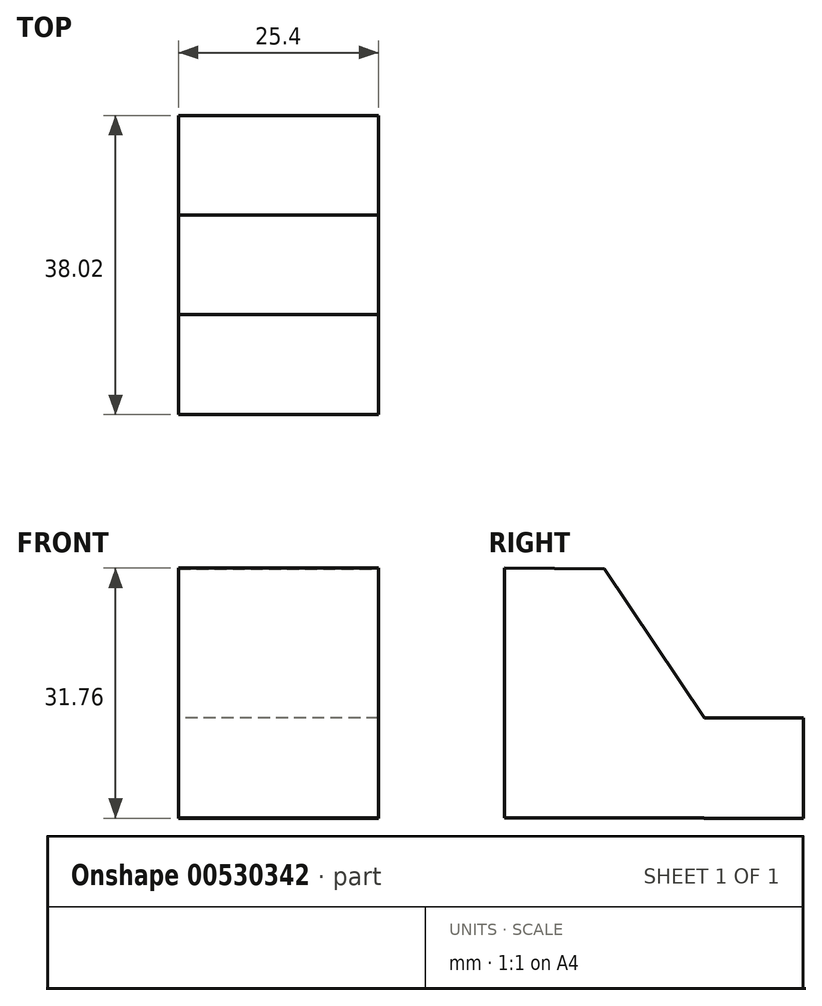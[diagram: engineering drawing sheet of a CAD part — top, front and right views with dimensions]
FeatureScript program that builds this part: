
annotation { "Feature Type Name" : "Feature", "Feature Type Description" : "" }
export const myFeature = defineFeature(function(context is Context, id is Id, definition is map)
    precondition{}
    {
        {
            var Q0;
            Q0=qCreatedBy(makeId("Right.planeOp"),FACE);
            var sketch = newSketch(context, id + "F0", { "sketchPlane" : qUnion([Q0])});
            skLineSegment(sketch, "E0", {"start": v(-45.87, 32.76) * mm, "end": v(-45.87, 1.01) * mm});
            skLineSegment(sketch, "E1", {"start": v(-45.87, 1.01) * mm, "end": v(-20.47, 1.01) * mm});
            skLineSegment(sketch, "E2", {"start": v(-20.47, 1.01) * mm, "end": v(-20.47, 32.56) * mm});
            skLineSegment(sketch, "E3", {"start": v(-45.87, 32.76) * mm, "end": v(-20.47, 32.56) * mm});
            skSolve(sketch);
        }
        {
            var Q0;
            Q0 = qSketchRegion(id + "F0", true);
            extrude(context, id + "F1", {"entities" : qUnion([Q0]), "depth" : 25.4 * mm, "offsetDistance" : 25.4 * mm});
        }
        {
            var Q0;
            Q0=makeQuery(id+"F1.opExtrude","CAP_FACE",FACE,{"disambiguationData":[OSD([sQuery(id+"F0.wireOp",EDGE,"E0"),sQuery(id+"F0.wireOp",EDGE,"E1"),sQuery(id+"F0.wireOp",EDGE,"E2"),sQuery(id+"F0.wireOp",EDGE,"E3")])],"isStart":false});
            var sketch = newSketch(context, id + "F2", { "sketchPlane" : qUnion([Q0])});
            skLineSegment(sketch, "E4", {"start": v(-33.17, 32.66) * mm, "end": v(-20.47, 13.71) * mm});
            skSolve(sketch);
        }
        {
            var Q0;
            Q0 = qSketchRegion(id + "F2", true);
            var Q1;
            {var subQ0=sQuery(id+"F2.wireOp",EDGE,"E4");Q1=makeQuery(id+"F2.imprint","IMPRINT",FACE,{"disambiguationData":[TD([[makeQuery(id+"F2.imprint","IMPRINT",EDGE,{"derivedFrom":subQ0}),1.0]])]});}
            extrude(context, id + "F3", {"entities" : qUnion([Q0, Q1]), "operationType" : NewBodyOperationType.REMOVE, "oppositeDirection" : true, "depth" : 25.4 * mm, "offsetDistance" : 25.4 * mm});
        }
        {
            var Q0;
            Q0=qCreatedBy(makeId("Right.planeOp"),FACE);
            var sketch = newSketch(context, id + "F4", { "sketchPlane" : qUnion([Q0])});
            skLineSegment(sketch, "E5", {"start": v(-20.54, 1) * mm, "end": v(-20.54, 13.74) * mm});
            skLineSegment(sketch, "E6", {"start": v(-20.54, 13.74) * mm, "end": v(-7.85, 13.74) * mm});
            skLineSegment(sketch, "E7", {"start": v(-20.54, 1) * mm, "end": v(-7.85, 1) * mm});
            skLineSegment(sketch, "E8", {"start": v(-7.85, 13.74) * mm, "end": v(-7.85, 1) * mm});
            skLineSegment(sketch, "E9", {"start": v(-20.54, 13.74) * mm, "end": v(-20.54, 1) * mm});
            skSolve(sketch);
        }
        {
            var Q0;
            Q0=makeQuery(id+"F4.imprint","IMPRINT",FACE,{"disambiguationData":[TD([[makeQuery(id+"F4.imprint","IMPRINT",EDGE,{"derivedFrom":sQuery(id+"F4.wireOp",EDGE,"E6")}),-1.0]])]});
            extrude(context, id + "F5", {"entities" : qUnion([Q0]), "operationType" : NewBodyOperationType.ADD, "depth" : 25.4 * mm, "offsetDistance" : 25.4 * mm});
        }
    });
